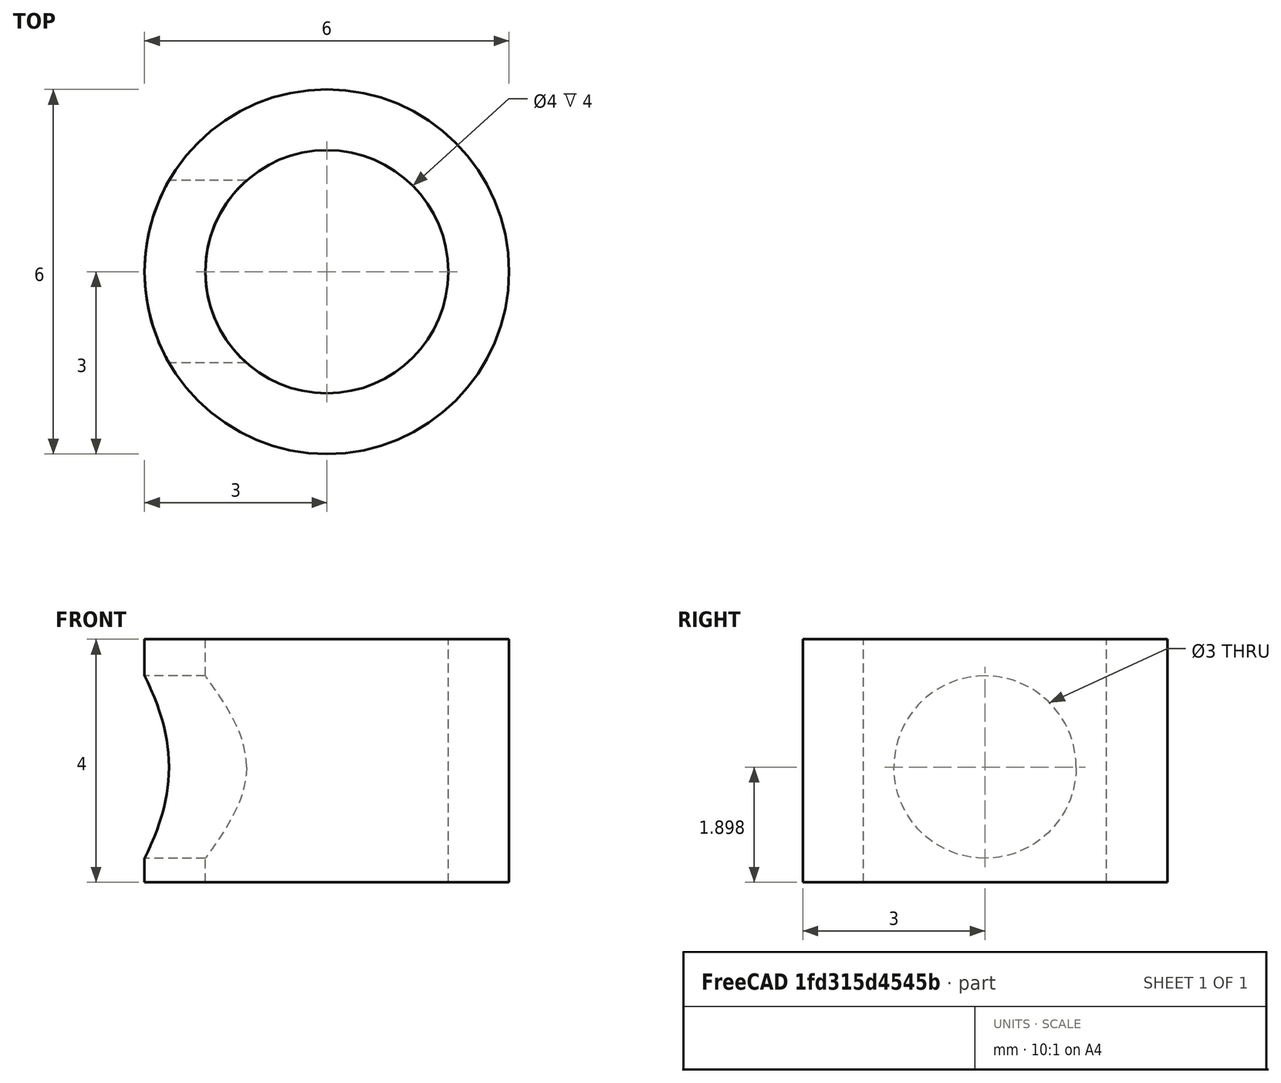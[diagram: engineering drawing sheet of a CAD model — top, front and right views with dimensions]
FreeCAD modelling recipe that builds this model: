
FCSTD DOCUMENT  (FreeCAD 0.15R4671 (Git))
Label: DowelPin_4mm_L4mm_setscrew_M3
License: All rights reserved
LicenseURL: http://es.wikipedia.org/wiki/Todos_los_derechos_reservados
objects: Part::Cylinder×2, Part::Cut×2, Sketcher::SketchObject×1, PartDesign::Pad×1
note: 7 computed .brp shape members not serialized (recipe doc carries the construction recipe); baked Part::Feature solids carry a one-line shape summary decoded from their .brp

FEATURE [Sketcher::SketchObject] Sketch
  sketch-geometry (1):
    g0: Circle CenterX=0 CenterY=0 CenterZ=0 NormalX=0 NormalY=0 NormalZ=1 Radius=3
  constraints (2):
    c: Coincident(g0,g-1)
    c: Radius(g0) = 3
FEATURE [PartDesign::Pad] Pad
  Length = 4
  Length2 = 100
  Sketch = -> Sketch
  Type = 0
FEATURE [Part::Cylinder] Cylinder  label="Cilindro"
  Angle = 360
  Height = 10
  Placement = pos=(1.07156,0,1.89758) rot=(0,-1,0;1.5708rad)
  Radius = 1.5
FEATURE [Part::Cylinder] Cylinder001  label="Cilindro001"
  Angle = 360
  Height = 10
  Placement = pos=(0,0,-3) rot=(0,0,1;0rad)
  Radius = 2
FEATURE [Part::Cut] Cut
  Base = -> Pad
  Tool = -> Cylinder001
FEATURE [Part::Cut] Cut001
  Base = -> Cut
  Tool = -> Cylinder
